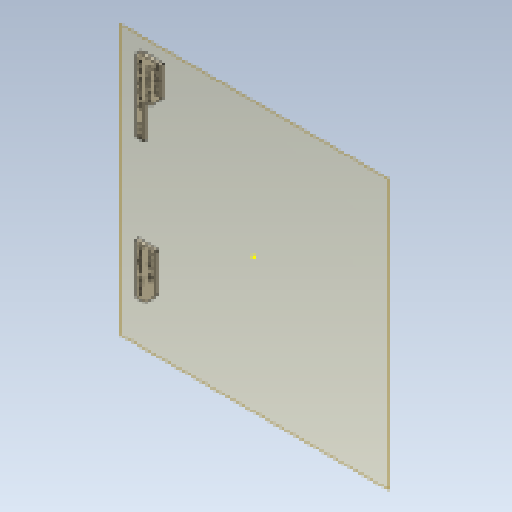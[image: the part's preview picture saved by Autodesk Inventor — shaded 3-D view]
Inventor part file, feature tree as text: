
AUTODESK INVENTOR PART (.ipt)
format: ipt  version: 2023 (Build 270158030, 158C)  size: 1,388,032 bytes
history: native  units: mm
features: other x3, plane x2, sketch x2, extrude x2, chamfer x1, reference x1
ambient origin geometry x8: Origin, YZ Plane, XZ Plane, XY Plane, X Axis, Y Axis, Z Axis, Center Point
bodies: Solid1 (feature_tree)
feature tree (11):
  plane  "Work Plane1"
  sketch  "Sketch1"  dims[d0=19.431275mm d1=23.65936mm]
  plane  "Work Plane2"
  extrude  "Extrusion1"  Depth=23.65936mm
  sketch  "Sketch2"  dims[d2=67.883459mm d3=8.354057mm d4=46.297087mm d5=37.541436mm d6=24.543837mm d7=70.0mm d8=10.0mm d9=0.0mm d10=10.0mm d11=2.0mm d12=45.0deg d19=2.0mm d20=0.0mm]
  chamfer  "Chamfer1"  Distance=8.354057mm
  extrude  "Extrusion2"  Depth=46.297087mm
  reference  "Reference1"
  other  "<userpath>\Documents\0004-inventor\3D-CAD-main\trebuchet\V4.0-trebuchet-printable.iam"
  other  "V4.0-trebuchet-printable.iam"
  other  "border:1"
